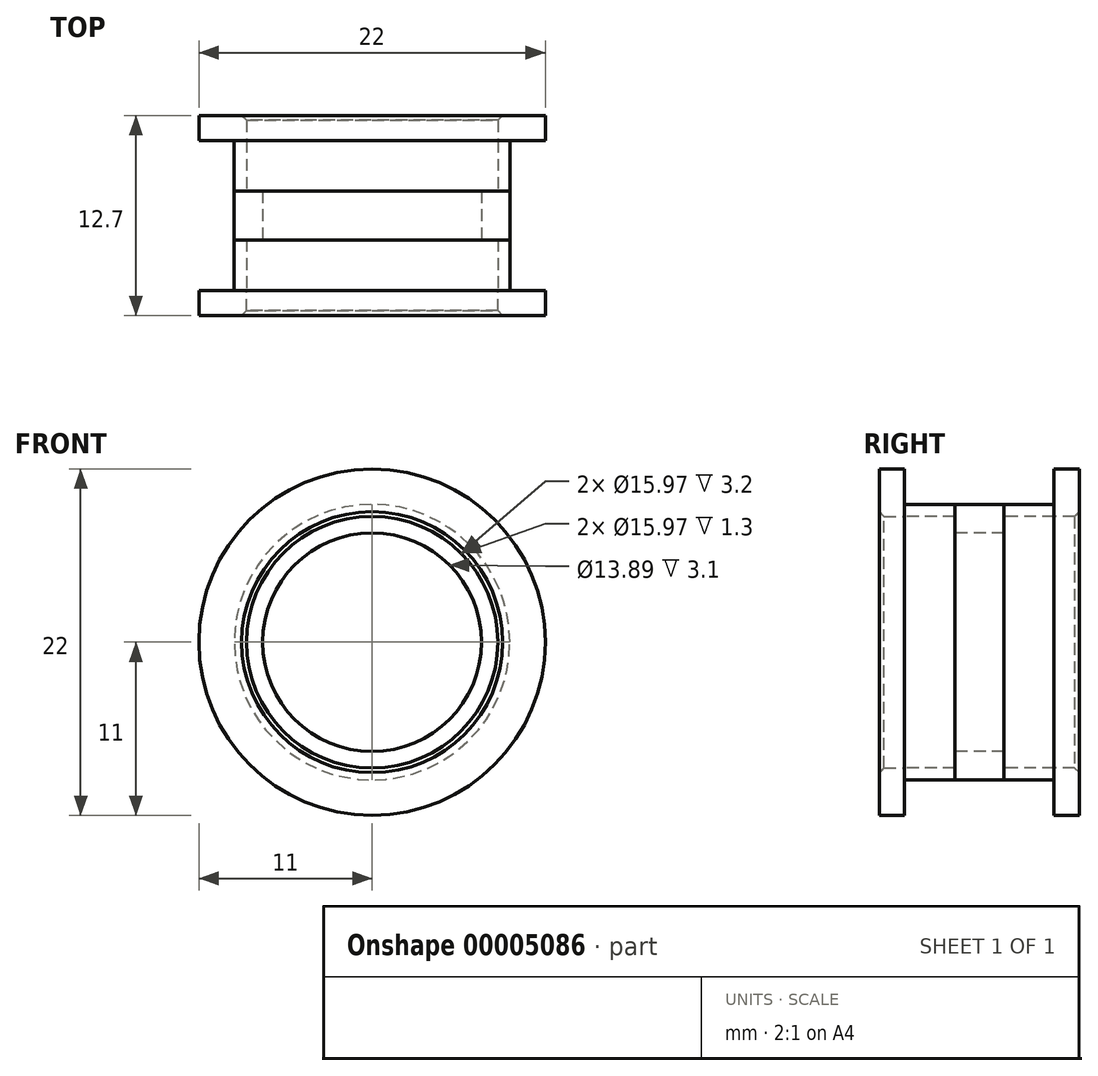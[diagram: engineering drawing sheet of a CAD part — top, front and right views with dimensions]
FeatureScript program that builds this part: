
annotation { "Feature Type Name" : "Feature", "Feature Type Description" : "" }
export const myFeature = defineFeature(function(context is Context, id is Id, definition is map)
    precondition{}
    {
        {
            var Q0;
            Q0=qCreatedBy(makeId("Front.planeOp"),FACE);
            var sketch = newSketch(context, id + "F0", { "sketchPlane" : qUnion([Q0])});
            skCircle(sketch, "E0", {"center": v(0, 0) * mm, "radius": 7.99 * mm});
            skCircle(sketch, "E1", {"center": v(0, 0) * mm, "radius": 11 * mm});
            skSolve(sketch);
        }
        {
            var Q0;
            Q0=makeQuery(id+"F0.imprint","IMPRINT",FACE,{"disambiguationData":[TD([[makeQuery(id+"F0.imprint","IMPRINT",EDGE,{"derivedFrom":sQuery(id+"F0.wireOp",EDGE,"E0")}),-1.0]])]});
            extrude(context, id + "F1", {"entities" : qUnion([Q0]), "depth" : 1.6 * mm});
        }
        {
            var Q0;
            Q0=makeQuery(id+"F1.opExtrude","CAP_FACE",FACE,{"disambiguationData":[OSD([sQuery(id+"F0.wireOp",EDGE,"E0"),sQuery(id+"F0.wireOp",EDGE,"E1")])],"isStart":true});
            var sketch = newSketch(context, id + "F2", { "sketchPlane" : qUnion([Q0])});
            skCircle(sketch, "E2", {"center": v(0, 0) * mm, "radius": 8.75 * mm});
            skCircle(sketch, "E3", {"center": v(0, 0) * mm, "radius": 7.99 * mm});
            skSolve(sketch);
        }
        {
            var Q0;
            Q0=makeQuery(id+"F2.imprint","IMPRINT",FACE,{"disambiguationData":[TD([[makeQuery(id+"F2.imprint","IMPRINT",EDGE,{"derivedFrom":sQuery(id+"F2.wireOp",EDGE,"E2")}),1.0]])]});
            extrude(context, id + "F3", {"entities" : qUnion([Q0]), "depth" : 3.2 * mm});
        }
        {
            var Q0;
            Q0=makeQuery(id+"F3.opExtrude","CAP_FACE",FACE,{"disambiguationData":[OSD([sQuery(id+"F2.wireOp",EDGE,"E2"),sQuery(id+"F2.wireOp",EDGE,"E3")])],"isStart":false});
            var sketch = newSketch(context, id + "F4", { "sketchPlane" : qUnion([Q0])});
            skCircle(sketch, "E4", {"center": v(0, 0) * mm, "radius": 6.95 * mm});
            skCircle(sketch, "E5", {"center": v(0, 0) * mm, "radius": 8.75 * mm});
            skSolve(sketch);
        }
        {
            var Q0;
            Q0=qSketchRegion(id+"F4",true);
            extrude(context, id + "F5", {"entities" : qUnion([Q0]), "depth" : 3.1 * mm});
        }
        {
            var Q0;
            Q0=makeQuery(id+"F5.opExtrude","CAP_FACE",FACE,{"disambiguationData":[OSD([sQuery(id+"F4.wireOp",EDGE,"E4"),sQuery(id+"F4.wireOp",EDGE,"E5")])],"isStart":false});
            var sketch = newSketch(context, id + "F6", { "sketchPlane" : qUnion([Q0])});
            skCircle(sketch, "E6", {"center": v(0, 0) * mm, "radius": 7.99 * mm});
            skCircle(sketch, "E7", {"center": v(0, 0) * mm, "radius": 8.75 * mm});
            skSolve(sketch);
        }
        {
            var Q0;
            Q0=makeQuery(id+"F6.imprint","IMPRINT",FACE,{"disambiguationData":[TD([[makeQuery(id+"F6.imprint","IMPRINT",EDGE,{"derivedFrom":sQuery(id+"F6.wireOp",EDGE,"E6")}),-1.0]])]});
            extrude(context, id + "F7", {"entities" : qUnion([Q0]), "depth" : 3.2 * mm});
        }
        {
            var Q0;
            Q0=makeQuery(id+"F7.opExtrude","CAP_FACE",FACE,{"disambiguationData":[OSD([sQuery(id+"F6.wireOp",EDGE,"E6"),sQuery(id+"F6.wireOp",EDGE,"E7")])],"isStart":false});
            var sketch = newSketch(context, id + "F8", { "sketchPlane" : qUnion([Q0])});
            skCircle(sketch, "E8", {"center": v(0, 0) * mm, "radius": 7.99 * mm});
            skCircle(sketch, "E9", {"center": v(0, 0) * mm, "radius": 11 * mm});
            skSolve(sketch);
        }
        {
            var Q0;
            Q0=qSketchRegion(id+"F8",true);
            extrude(context, id + "F9", {"entities" : qUnion([Q0]), "depth" : 1.6 * mm});
        }
        {
            var Q0;
            Q0=makeQuery(id+"F9.opExtrude","CAP_EDGE",EDGE,{"disambiguationData":[OSD([sQuery(id+"F8.wireOp",EDGE,"E8")])],"isStart":false});
            chamfer(context, id + "F10", {"entities" : qUnion([Q0]), "width" : 0.3 * mm, "tangentPropagation" : true});
        }
        {
            var Q0;
            Q0=makeQuery(id+"F1.opExtrude","CAP_EDGE",EDGE,{"disambiguationData":[OSD([sQuery(id+"F0.wireOp",EDGE,"E0")])],"isStart":false});
            chamfer(context, id + "F11", {"entities" : qUnion([Q0]), "width" : 0.3 * mm, "tangentPropagation" : true});
        }
    });
